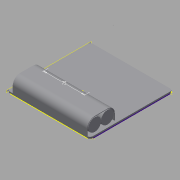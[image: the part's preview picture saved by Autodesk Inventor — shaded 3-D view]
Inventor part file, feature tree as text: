
AUTODESK INVENTOR PART (.ipt)
format: ipt  version: 2015 (Build 190159000, 159)  size: 202,240 bytes
history: native  units: in
note: dims shown in document units (in); Inventor stores cm internally (conversion verified against a paired STEP export)
features: sketch x12, extrude x9, plane x5, fillet x4
ambient origin geometry x8: Origin, YZ Plane, XZ Plane, XY Plane, X Axis, Y Axis, Z Axis, Center Point
bodies: Solid1 (feature_tree)
feature tree (30):
  extrude  "Extrusion1"  Depth=0.1181in TaperAngle=0.0deg
  plane  "Work Plane1"
  extrude  "Extrusion2"  Depth=0.3937in
  sketch  "Sketch4"  dims[d13=0.4528in d14=0.4528in]
  sketch  "Sketch5"  dims[d15=0.9055in d16=5.315in d17=0.0in]
  extrude  "Extrusion3"  Depth=0.4528in
  plane  "Work Plane2"
  extrude  "Extrusion5"  Depth=5.315in TaperAngle=0.0deg
  plane  "Work Plane3"
  extrude  "Extrusion6"  Depth=0.0394in
  extrude  "Extrusion7"  TaperAngle=0.0deg  [1 undecoded]
  plane  "Work Plane4"
  extrude  "Extrusion8"  TaperAngle=0.0deg  [1 undecoded]
  extrude  "Extrusion9"  Depth=0.1969in TaperAngle=0.0deg
  fillet  "Fillet1"  [1 undecoded]
  fillet  "Fillet2"  Radius=0.1969in
  fillet  "Fillet3"  Radius=0.315in
  fillet  "Fillet4"  Radius=0.1969in
  sketch  "Sketch13"  dims[d47=2.9528in]
  plane  "Work Plane5"
  extrude  "Extrusion10"  Depth=0.1969in
  sketch  "Sketch1"  dims[d4=0.3937in d5=0.1181in d6=0.0in]
  sketch  "Sketch3"  dims[d11=2.9528in d12=0.3937in]
  sketch  "Sketch6"  dims[d20=0.4921in d21=0.0394in]
  sketch  "Sketch8"  dims[d22=5.315in d23=0.0in d30=0.0in]
  sketch  "Sketch9"  dims[d31=0.315in d32=0.0in d33=0.0in]
  sketch  "Sketch10"  dims[d34=0.1969in d35=0.0in d36=0.1969in d37=0.0in d38=0.0in d39=0.1969in d40=0.0in d41=0.315in d42=0.0in d43=0.1969in]
  sketch  "Sketch11"  dims[d44=0.1969in d45=0.1969in]
  sketch  "Sketch12"  dims[d46=0.1969in]
  sketch  "Sketch14"  dims[d48=0.0in d49=0.3012in d50=0.3012in d52=0.6693in d53=0.0787in d54=0.0787in d55=0.3346in d56=0.7087in d57=0.0in]
note: 3 required parameter values undecoded (feature->parameter linkage not recoverable at this tier; creation-order binding heuristic only, values carry confidence <= 0.55)
